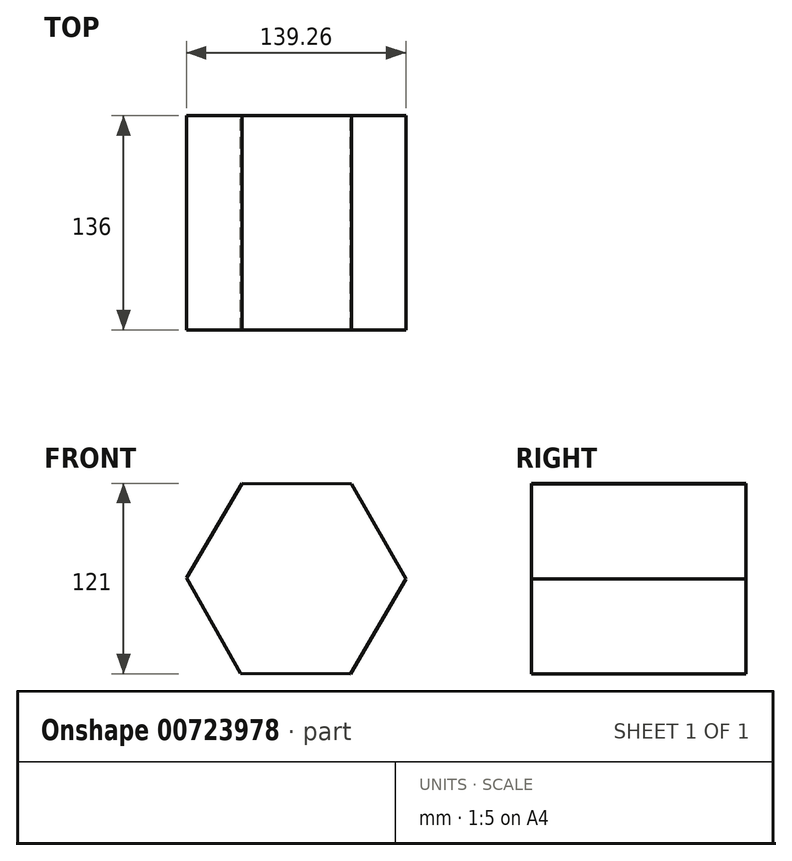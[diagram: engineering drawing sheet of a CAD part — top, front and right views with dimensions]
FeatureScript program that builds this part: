
annotation { "Feature Type Name" : "Feature", "Feature Type Description" : "" }
export const myFeature = defineFeature(function(context is Context, id is Id, definition is map)
    precondition{}
    {
        {
            var Q0;
            Q0=qCreatedBy(makeId("Front.planeOp"),FACE);
            var sketch = newSketch(context, id + "F0", { "sketchPlane" : qUnion([Q0])});
            skCircle(sketch, "E0.cCircle", {"center": v(0, 0) * mm, "radius": 60.3 * mm, "construction": true});
            skLineSegment(sketch, "E0.0", {"start": v(-35.15, -60.1) * mm, "end": v(-69.63, 0.4) * mm});
            skLineSegment(sketch, "E0.1", {"start": v(-69.63, 0.4) * mm, "end": v(-34.48, 60.5) * mm});
            skLineSegment(sketch, "E0.2", {"start": v(-34.48, 60.5) * mm, "end": v(35.15, 60.1) * mm});
            skLineSegment(sketch, "E0.3", {"start": v(35.15, 60.1) * mm, "end": v(69.63, -0.4) * mm});
            skLineSegment(sketch, "E0.4", {"start": v(69.63, -0.4) * mm, "end": v(34.48, -60.5) * mm});
            skLineSegment(sketch, "E0.5", {"start": v(34.48, -60.5) * mm, "end": v(-35.15, -60.1) * mm});
            skPoint(sketch, "E0.0.midPoint", {"position": v(-52.4, -29.86) * mm});
            skSolve(sketch);
        }
        {
            var Q0;
            Q0=makeQuery(id+"F0.imprint","IMPRINT",FACE,{"disambiguationData":[TD([[makeQuery(id+"F0.imprint","IMPRINT",EDGE,{"derivedFrom":sQuery(id+"F0.wireOp",EDGE,"E0.0")}),-1.0]])]});
            extrude(context, id + "F1", {"entities" : qUnion([Q0]), "depth" : 136 * mm, "offsetDistance" : 25 * mm});
        }
    });
